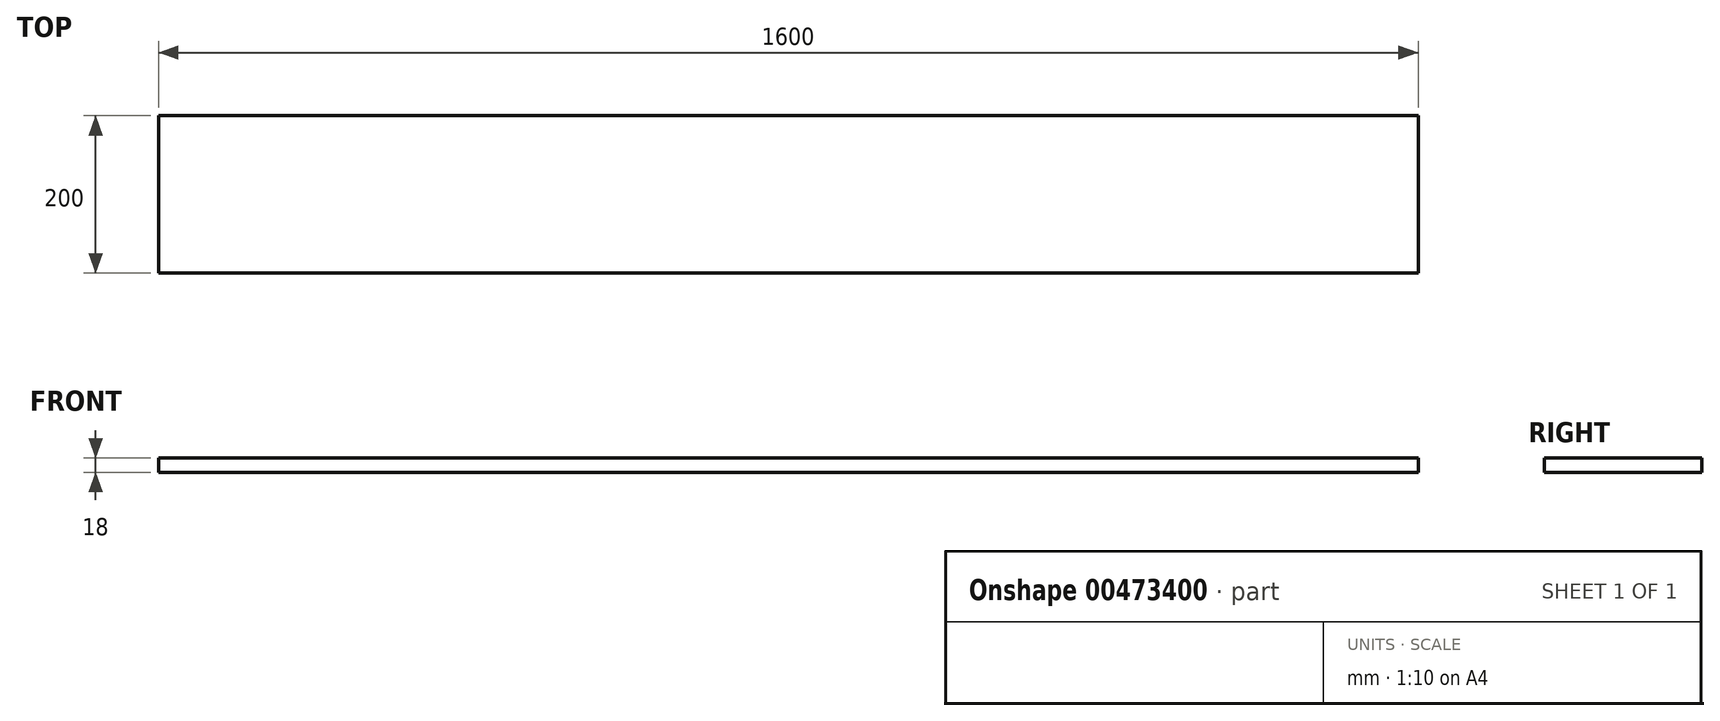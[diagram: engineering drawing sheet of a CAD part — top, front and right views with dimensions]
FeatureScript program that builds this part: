
annotation { "Feature Type Name" : "Feature", "Feature Type Description" : "" }
export const myFeature = defineFeature(function(context is Context, id is Id, definition is map)
    precondition{}
    {
        {
            var Q0;
            Q0=qCreatedBy(makeId("Top.planeOp"),FACE);
            var sketch = newSketch(context, id + "F0", { "sketchPlane" : qUnion([Q0])});
            skLineSegment(sketch, "E0.bottom", {"start": v(0, 0) * mm, "end": v(1600, 0) * mm});
            skLineSegment(sketch, "E0.top", {"start": v(0, 200) * mm, "end": v(1600, 200) * mm});
            skLineSegment(sketch, "E0.left", {"start": v(0, 0) * mm, "end": v(0, 200) * mm});
            skLineSegment(sketch, "E0.right", {"start": v(1600, 0) * mm, "end": v(1600, 200) * mm});
            skSolve(sketch);
        }
        {
            var Q0;
            Q0 = qSketchRegion(id + "F0", true);
            extrude(context, id + "F1", {"entities" : qUnion([Q0]), "depth" : 18 * mm});
        }
    });
